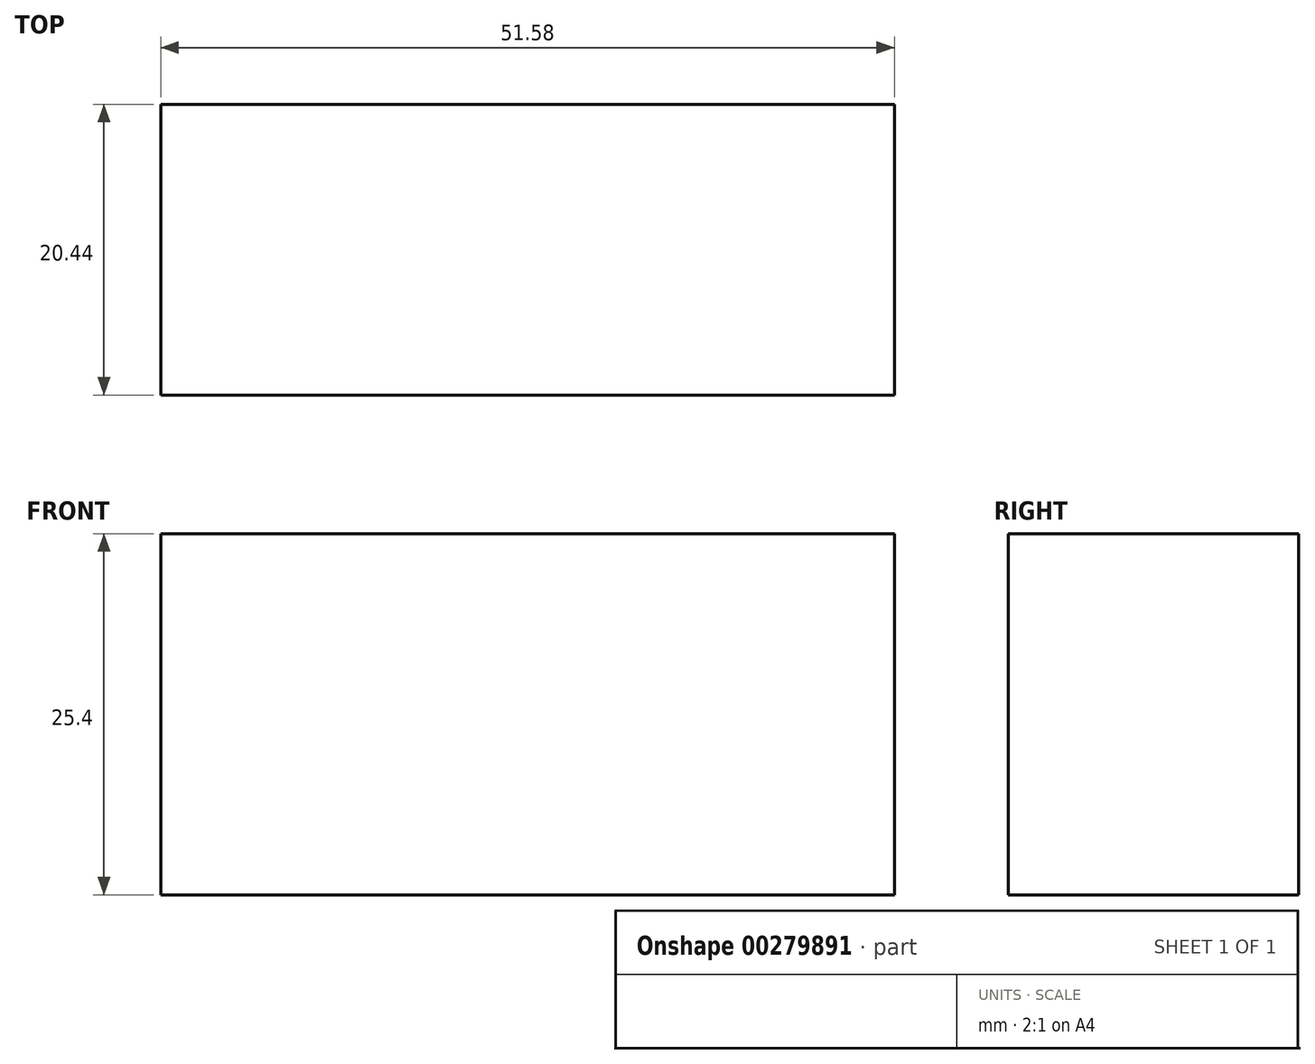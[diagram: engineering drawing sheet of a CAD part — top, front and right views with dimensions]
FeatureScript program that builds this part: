
annotation { "Feature Type Name" : "Feature", "Feature Type Description" : "" }
export const myFeature = defineFeature(function(context is Context, id is Id, definition is map)
    precondition{}
    {
        {
            var Q0;
            Q0=qCreatedBy(makeId("Top.planeOp"),FACE);
            var sketch = newSketch(context, id + "F0", { "sketchPlane" : qUnion([Q0])});
            skLineSegment(sketch, "E0.bottom", {"start": v(-28.15, -10.22) * mm, "end": v(-79.73, -10.22) * mm});
            skLineSegment(sketch, "E0.top", {"start": v(-28.15, 10.22) * mm, "end": v(-79.73, 10.22) * mm});
            skLineSegment(sketch, "E0.left", {"start": v(-28.15, -10.22) * mm, "end": v(-28.15, 10.22) * mm});
            skLineSegment(sketch, "E0.right", {"start": v(-79.73, -10.22) * mm, "end": v(-79.73, 10.22) * mm});
            skPoint(sketch, "E0.middle", {"position": v(-53.94, 0) * mm});
            skSolve(sketch);
        }
        {
            var Q0;
            Q0 = qSketchRegion(id + "F0", true);
            extrude(context, id + "F1", {"entities" : qUnion([Q0]), "depth" : 25.4 * mm});
        }
    });
